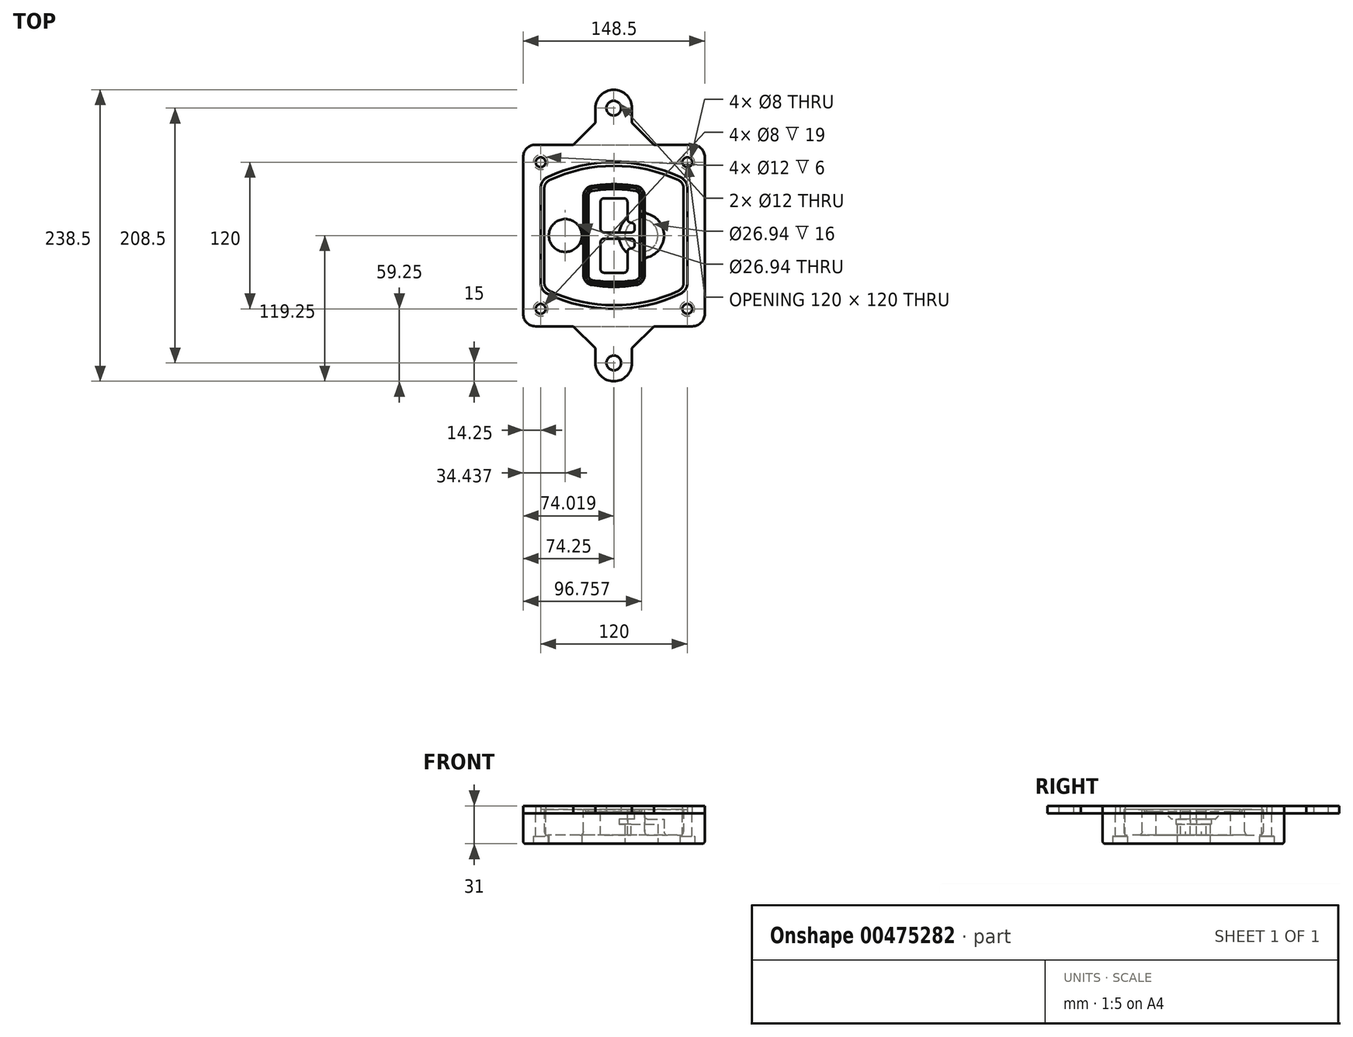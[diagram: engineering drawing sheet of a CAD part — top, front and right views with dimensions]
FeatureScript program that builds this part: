
annotation { "Feature Type Name" : "Feature", "Feature Type Description" : "" }
export const myFeature = defineFeature(function(context is Context, id is Id, definition is map)
    precondition{}
    {
        {
            var Q0;
            Q0=qCreatedBy(makeId("Top.planeOp"),FACE);
            var sketch = newSketch(context, id + "F0", { "sketchPlane" : qUnion([Q0])});
            skPoint(sketch, "E0.rect.middle", {"position": v(0, 0) * mm});
            skLineSegment(sketch, "E1.bottom", {"start": v(-64.25, -74.25) * mm, "end": v(64.25, -74.25) * mm});
            skLineSegment(sketch, "E1.top", {"start": v(-64.25, 74.25) * mm, "end": v(64.25, 74.25) * mm});
            skLineSegment(sketch, "E1.left", {"start": v(-74.25, -64.25) * mm, "end": v(-74.25, 64.25) * mm});
            skLineSegment(sketch, "E1.right", {"start": v(74.25, -64.25) * mm, "end": v(74.25, 64.25) * mm});
            skLineSegment(sketch, "E2", {"start": v(-74.25, 74.25) * mm, "end": v(74.25, -74.25) * mm, "construction": true});
            skLineSegment(sketch, "E3", {"start": v(74.25, 74.25) * mm, "end": v(-74.25, -74.25) * mm, "construction": true});
            skCircle(sketch, "E4", {"center": v(-60, 60) * mm, "radius": 4 * mm});
            skCircle(sketch, "E5", {"center": v(60, 60) * mm, "radius": 4 * mm});
            skCircle(sketch, "E6", {"center": v(60, -60) * mm, "radius": 4 * mm});
            skCircle(sketch, "E7", {"center": v(-60, -60) * mm, "radius": 4 * mm});
            skLineSegment(sketch, "E8", {"start": v(-60, 60) * mm, "end": v(60, 60) * mm, "construction": true});
            skLineSegment(sketch, "E9", {"start": v(60, 60) * mm, "end": v(60, -60) * mm, "construction": true});
            skLineSegment(sketch, "E10", {"start": v(60, -60) * mm, "end": v(-60, -60) * mm, "construction": true});
            skLineSegment(sketch, "E11", {"start": v(-60, -60) * mm, "end": v(-60, 60) * mm, "construction": true});
            skLineSegment(sketch, "E12", {"start": v(-60, 38.83) * mm, "end": v(-60, -38.83) * mm});
            skLineSegment(sketch, "E13", {"start": v(60, 38.83) * mm, "end": v(60, -38.83) * mm});
            skArc(sketch, "E14", {"start": v(54.26, 47.88) * mm, "mid": v(0, 60) * mm, "end": v(-54.26, 47.88) * mm});
            skArc(sketch, "E15", {"start": v(-54.26, -47.88) * mm, "mid": v(0, -60) * mm, "end": v(54.26, -47.88) * mm});
            skLineSegment(sketch, "E16", {"start": v(-60, 0) * mm, "end": v(60, 0) * mm, "construction": true});
            skPoint(sketch, "E17.visualSharp", {"position": v(-60, -45) * mm});
            skArc(sketch, "E17.filletArc", {"start": v(-60, -38.83) * mm, "mid": v(-58.44, -44.2) * mm, "end": v(-54.26, -47.88) * mm});
            skPoint(sketch, "E18.visualSharp", {"position": v(-60, 45) * mm});
            skArc(sketch, "E18.filletArc", {"start": v(-54.26, 47.88) * mm, "mid": v(-58.44, 44.2) * mm, "end": v(-60, 38.83) * mm});
            skPoint(sketch, "E19.visualSharp", {"position": v(60, 45) * mm});
            skArc(sketch, "E19.filletArc", {"start": v(60, 38.83) * mm, "mid": v(58.44, 44.2) * mm, "end": v(54.26, 47.88) * mm});
            skPoint(sketch, "E20.visualSharp", {"position": v(60, -45) * mm});
            skArc(sketch, "E20.filletArc", {"start": v(54.26, -47.88) * mm, "mid": v(58.44, -44.2) * mm, "end": v(60, -38.83) * mm});
            skPoint(sketch, "E21.visualSharp", {"position": v(-74.25, 74.25) * mm});
            skArc(sketch, "E21.filletArc", {"start": v(-64.25, 74.25) * mm, "mid": v(-71.32, 71.32) * mm, "end": v(-74.25, 64.25) * mm});
            skPoint(sketch, "E22.visualSharp", {"position": v(74.25, 74.25) * mm});
            skArc(sketch, "E22.filletArc", {"start": v(74.25, 64.25) * mm, "mid": v(71.32, 71.32) * mm, "end": v(64.25, 74.25) * mm});
            skPoint(sketch, "E23.visualSharp", {"position": v(74.25, -74.25) * mm});
            skArc(sketch, "E23.filletArc", {"start": v(64.25, -74.25) * mm, "mid": v(71.32, -71.32) * mm, "end": v(74.25, -64.25) * mm});
            skPoint(sketch, "E24.visualSharp", {"position": v(-74.25, -74.25) * mm});
            skArc(sketch, "E24.filletArc", {"start": v(-74.25, -64.25) * mm, "mid": v(-71.32, -71.32) * mm, "end": v(-64.25, -74.25) * mm});
            skArc(sketch, "E25.0", {"start": v(57, 38.83) * mm, "mid": v(55.9, 42.58) * mm, "end": v(52.98, 45.17) * mm});
            skLineSegment(sketch, "E25.1", {"start": v(57, 38.83) * mm, "end": v(57, -38.83) * mm});
            skArc(sketch, "E25.2", {"start": v(52.98, -45.17) * mm, "mid": v(55.9, -42.58) * mm, "end": v(57, -38.83) * mm});
            skArc(sketch, "E25.3", {"start": v(-52.98, -45.17) * mm, "mid": v(0, -57) * mm, "end": v(52.98, -45.17) * mm});
            skArc(sketch, "E25.4", {"start": v(-57, -38.83) * mm, "mid": v(-55.9, -42.58) * mm, "end": v(-52.98, -45.17) * mm});
            skArc(sketch, "E25.5", {"start": v(52.98, 45.17) * mm, "mid": v(0, 57) * mm, "end": v(-52.98, 45.17) * mm});
            skLineSegment(sketch, "E25.6", {"start": v(-57, 38.83) * mm, "end": v(-57, -38.83) * mm});
            skArc(sketch, "E25.7", {"start": v(-52.98, 45.17) * mm, "mid": v(-55.9, 42.58) * mm, "end": v(-57, 38.83) * mm});
            skArc(sketch, "E26.0", {"start": v(-55.96, 51.5) * mm, "mid": v(-61.82, 46.33) * mm, "end": v(-64, 38.83) * mm});
            skArc(sketch, "E26.1", {"start": v(55.96, 51.5) * mm, "mid": v(0, 64) * mm, "end": v(-55.96, 51.5) * mm});
            skArc(sketch, "E26.2", {"start": v(64, 38.83) * mm, "mid": v(61.82, 46.33) * mm, "end": v(55.96, 51.5) * mm});
            skLineSegment(sketch, "E26.3", {"start": v(64, 38.83) * mm, "end": v(64, -38.83) * mm});
            skArc(sketch, "E26.4", {"start": v(55.96, -51.5) * mm, "mid": v(61.82, -46.33) * mm, "end": v(64, -38.83) * mm});
            skLineSegment(sketch, "E26.5", {"start": v(-64, 38.83) * mm, "end": v(-64, -38.83) * mm});
            skArc(sketch, "E26.6", {"start": v(-55.96, -51.5) * mm, "mid": v(0, -64) * mm, "end": v(55.96, -51.5) * mm});
            skArc(sketch, "E26.7", {"start": v(-64, -38.83) * mm, "mid": v(-61.82, -46.33) * mm, "end": v(-55.96, -51.5) * mm});
            skSolve(sketch);
        }
        {
            var Q0;
            Q0=makeQuery(id+"F0.imprint","IMPRINT",FACE,{"disambiguationData":[TD([[makeQuery(id+"F0.imprint","IMPRINT",EDGE,{"derivedFrom":sQuery(id+"F0.wireOp",EDGE,"E1.bottom")}),1.0]])]});
            var Q1;
            Q1=makeQuery(id+"F0.imprint","IMPRINT",FACE,{"disambiguationData":[TD([[makeQuery(id+"F0.imprint","IMPRINT",EDGE,{"derivedFrom":sQuery(id+"F0.wireOp",EDGE,"E12")}),1.0]])]});
            var Q2;
            Q2=makeQuery(id+"F0.imprint","IMPRINT",FACE,{"disambiguationData":[TD([[makeQuery(id+"F0.imprint","IMPRINT",EDGE,{"derivedFrom":sQuery(id+"F0.wireOp",EDGE,"E25.0")}),1.0]])]});
            var Q3;
            Q3=makeQuery(id+"F0.imprint","IMPRINT",FACE,{"disambiguationData":[TD([[makeQuery(id+"F0.imprint","IMPRINT",EDGE,{"derivedFrom":sQuery(id+"F0.wireOp",EDGE,"E12")}),-1.0]])]});
            extrude(context, id + "F1", {"entities" : qUnion([Q0, Q1, Q2, Q3]), "oppositeDirection" : true, "depth" : 25 * mm});
        }
        {
            var Q0;
            Q0=makeQuery(id+"F0.imprint","IMPRINT",FACE,{"disambiguationData":[TD([[makeQuery(id+"F0.imprint","IMPRINT",EDGE,{"derivedFrom":sQuery(id+"F0.wireOp",EDGE,"E12")}),1.0]])]});
            extrude(context, id + "F2", {"entities" : qUnion([Q0]), "operationType" : NewBodyOperationType.ADD, "depth" : 3 * mm});
        }
        {
            var Q0;
            Q0=makeQuery(id+"F0.imprint","IMPRINT",FACE,{"disambiguationData":[TD([[makeQuery(id+"F0.imprint","IMPRINT",EDGE,{"derivedFrom":sQuery(id+"F0.wireOp",EDGE,"E25.0")}),1.0]])]});
            extrude(context, id + "F3", {"entities" : qUnion([Q0]), "operationType" : NewBodyOperationType.REMOVE, "oppositeDirection" : true, "depth" : 18 * mm});
        }
        {
            var Q0;
            Q0=makeQuery(id+"F2.opExtrude","CAP_FACE",FACE,{"disambiguationData":[OSD([sQuery(id+"F0.wireOp",EDGE,"E12"),sQuery(id+"F0.wireOp",EDGE,"E13"),sQuery(id+"F0.wireOp",EDGE,"E14"),sQuery(id+"F0.wireOp",EDGE,"E15"),sQuery(id+"F0.wireOp",EDGE,"E17.filletArc"),sQuery(id+"F0.wireOp",EDGE,"E18.filletArc"),sQuery(id+"F0.wireOp",EDGE,"E19.filletArc"),sQuery(id+"F0.wireOp",EDGE,"E20.filletArc"),sQuery(id+"F0.wireOp",EDGE,"E25.0"),sQuery(id+"F0.wireOp",EDGE,"E25.1"),sQuery(id+"F0.wireOp",EDGE,"E25.2"),sQuery(id+"F0.wireOp",EDGE,"E25.3"),sQuery(id+"F0.wireOp",EDGE,"E25.4"),sQuery(id+"F0.wireOp",EDGE,"E25.5"),sQuery(id+"F0.wireOp",EDGE,"E25.6"),sQuery(id+"F0.wireOp",EDGE,"E25.7")])],"isStart":false});
            var sketch = newSketch(context, id + "F4", { "sketchPlane" : qUnion([Q0])});
            skArc(sketch, "E27.0", {"start": v(-18.34, -40.45) * mm, "mid": v(0, -42) * mm, "end": v(18.34, -40.45) * mm});
            skArc(sketch, "E28.0", {"start": v(18.34, 40.45) * mm, "mid": v(0, 42) * mm, "end": v(-18.34, 40.45) * mm});
            skLineSegment(sketch, "E29", {"start": v(-25, 32.57) * mm, "end": v(-25, -32.57) * mm});
            skLineSegment(sketch, "E30", {"start": v(25, 32.57) * mm, "end": v(25, -32.57) * mm});
            skLineSegment(sketch, "E31", {"start": v(-25, 39.1) * mm, "end": v(25, 39.1) * mm, "construction": true});
            skLineSegment(sketch, "E32", {"start": v(-25, -39.1) * mm, "end": v(25, -39.1) * mm, "construction": true});
            skPoint(sketch, "E33.visualSharp", {"position": v(-25, 39.1) * mm});
            skArc(sketch, "E33.filletArc", {"start": v(-18.34, 40.45) * mm, "mid": v(-23.11, 37.73) * mm, "end": v(-25, 32.57) * mm});
            skPoint(sketch, "E34.visualSharp", {"position": v(25, 39.1) * mm});
            skArc(sketch, "E34.filletArc", {"start": v(25, 32.57) * mm, "mid": v(23.11, 37.73) * mm, "end": v(18.34, 40.45) * mm});
            skPoint(sketch, "E35.visualSharp", {"position": v(25, -39.1) * mm});
            skArc(sketch, "E35.filletArc", {"start": v(18.34, -40.45) * mm, "mid": v(23.11, -37.73) * mm, "end": v(25, -32.57) * mm});
            skPoint(sketch, "E36.visualSharp", {"position": v(-25, -39.1) * mm});
            skArc(sketch, "E36.filletArc", {"start": v(-25, -32.57) * mm, "mid": v(-23.11, -37.73) * mm, "end": v(-18.34, -40.45) * mm});
            skArc(sketch, "E37.0", {"start": v(52.98, 45.17) * mm, "mid": v(0, 57) * mm, "end": v(-52.98, 45.17) * mm});
            skArc(sketch, "E37.1", {"start": v(-52.98, 45.17) * mm, "mid": v(-55.9, 42.58) * mm, "end": v(-57, 38.83) * mm});
            skLineSegment(sketch, "E37.2", {"start": v(-57, 38.83) * mm, "end": v(-57, -38.83) * mm});
            skArc(sketch, "E37.3", {"start": v(-57, -38.83) * mm, "mid": v(-55.9, -42.58) * mm, "end": v(-52.98, -45.17) * mm});
            skArc(sketch, "E37.4", {"start": v(-52.98, -45.17) * mm, "mid": v(0, -57) * mm, "end": v(52.98, -45.17) * mm});
            skArc(sketch, "E37.5", {"start": v(52.98, -45.17) * mm, "mid": v(55.9, -42.58) * mm, "end": v(57, -38.83) * mm});
            skLineSegment(sketch, "E37.6", {"start": v(57, 38.83) * mm, "end": v(57, -38.83) * mm});
            skArc(sketch, "E37.7", {"start": v(57, 38.83) * mm, "mid": v(55.9, 42.58) * mm, "end": v(52.98, 45.17) * mm});
            skLineSegment(sketch, "E38.0", {"start": v(23, 32.57) * mm, "end": v(23, -32.57) * mm});
            skArc(sketch, "E38.1", {"start": v(18, -38.48) * mm, "mid": v(21.58, -36.44) * mm, "end": v(23, -32.57) * mm});
            skArc(sketch, "E38.2", {"start": v(-18, -38.48) * mm, "mid": v(0, -40) * mm, "end": v(18, -38.48) * mm});
            skArc(sketch, "E38.3", {"start": v(-23, -32.57) * mm, "mid": v(-21.58, -36.44) * mm, "end": v(-18, -38.48) * mm});
            skLineSegment(sketch, "E38.4", {"start": v(-23, 32.57) * mm, "end": v(-23, -32.57) * mm});
            skArc(sketch, "E38.5", {"start": v(23, 32.57) * mm, "mid": v(21.58, 36.44) * mm, "end": v(18, 38.48) * mm});
            skArc(sketch, "E38.6", {"start": v(-18, 38.48) * mm, "mid": v(-21.58, 36.44) * mm, "end": v(-23, 32.57) * mm});
            skArc(sketch, "E38.7", {"start": v(18, 38.48) * mm, "mid": v(0, 40) * mm, "end": v(-18, 38.48) * mm});
            skArc(sketch, "E39.0", {"start": v(21, 32.57) * mm, "mid": v(20.06, 35.15) * mm, "end": v(17.67, 36.5) * mm});
            skLineSegment(sketch, "E39.1", {"start": v(21, 32.57) * mm, "end": v(21, -32.57) * mm});
            skArc(sketch, "E39.2", {"start": v(17.67, -36.5) * mm, "mid": v(20.06, -35.15) * mm, "end": v(21, -32.57) * mm});
            skArc(sketch, "E39.3", {"start": v(-17.67, -36.5) * mm, "mid": v(0, -38) * mm, "end": v(17.67, -36.5) * mm});
            skArc(sketch, "E39.4", {"start": v(-21, -32.57) * mm, "mid": v(-20.06, -35.15) * mm, "end": v(-17.67, -36.5) * mm});
            skArc(sketch, "E39.5", {"start": v(17.67, 36.5) * mm, "mid": v(0, 38) * mm, "end": v(-17.67, 36.5) * mm});
            skLineSegment(sketch, "E39.6", {"start": v(-21, 32.57) * mm, "end": v(-21, -32.57) * mm});
            skArc(sketch, "E39.7", {"start": v(-17.67, 36.5) * mm, "mid": v(-20.06, 35.15) * mm, "end": v(-21, 32.57) * mm});
            skLineSegment(sketch, "E40", {"start": v(-25, 0) * mm, "end": v(25, 0) * mm, "construction": true});
            skLineSegment(sketch, "E41", {"start": v(-11, 5.5) * mm, "end": v(-11, 27.5) * mm});
            skLineSegment(sketch, "E42", {"start": v(-8, 30.5) * mm, "end": v(8, 30.5) * mm});
            skLineSegment(sketch, "E43", {"start": v(11, 27.5) * mm, "end": v(11, 13.5) * mm});
            skLineSegment(sketch, "E44", {"start": v(14, 10.5) * mm, "end": v(14, 10.5) * mm});
            skLineSegment(sketch, "E45", {"start": v(17, 7.5) * mm, "end": v(17, 5.5) * mm});
            skLineSegment(sketch, "E46", {"start": v(14, 2.5) * mm, "end": v(-8, 2.5) * mm});
            skPoint(sketch, "E47.visualSharp", {"position": v(-11, 30.5) * mm});
            skArc(sketch, "E47.filletArc", {"start": v(-8, 30.5) * mm, "mid": v(-10.12, 29.62) * mm, "end": v(-11, 27.5) * mm});
            skPoint(sketch, "E48.visualSharp", {"position": v(11, 30.5) * mm});
            skArc(sketch, "E48.filletArc", {"start": v(11, 27.5) * mm, "mid": v(10.12, 29.62) * mm, "end": v(8, 30.5) * mm});
            skPoint(sketch, "E49.visualSharp", {"position": v(11, 10.5) * mm});
            skArc(sketch, "E49.filletArc", {"start": v(11, 13.5) * mm, "mid": v(11.88, 11.38) * mm, "end": v(14, 10.5) * mm});
            skPoint(sketch, "E50.visualSharp", {"position": v(17, 10.5) * mm});
            skArc(sketch, "E50.filletArc", {"start": v(17, 7.5) * mm, "mid": v(16.12, 9.62) * mm, "end": v(14, 10.5) * mm});
            skPoint(sketch, "E51.visualSharp", {"position": v(17, 2.5) * mm});
            skArc(sketch, "E51.filletArc", {"start": v(14, 2.5) * mm, "mid": v(16.12, 3.38) * mm, "end": v(17, 5.5) * mm});
            skPoint(sketch, "E52.visualSharp", {"position": v(-11, 2.5) * mm});
            skArc(sketch, "E52.filletArc", {"start": v(-11, 5.5) * mm, "mid": v(-10.12, 3.38) * mm, "end": v(-8, 2.5) * mm});
            skLineSegment(sketch, "E53.0.MirrorCS", {"start": v(14, -2.5) * mm, "end": v(-8, -2.5) * mm});
            skArc(sketch, "E54.0.MirrorCS", {"start": v(-11, -5.5) * mm, "mid": v(-10.12, -3.38) * mm, "end": v(-8, -2.5) * mm});
            skLineSegment(sketch, "E55.0.MirrorCS", {"start": v(-11, -5.5) * mm, "end": v(-11, -27.5) * mm});
            skArc(sketch, "E56.0.MirrorCS", {"start": v(-8, -30.5) * mm, "mid": v(-10.12, -29.62) * mm, "end": v(-11, -27.5) * mm});
            skLineSegment(sketch, "E57.0.MirrorCS", {"start": v(-8, -30.5) * mm, "end": v(8, -30.5) * mm});
            skArc(sketch, "E58.0.MirrorCS", {"start": v(11, -27.5) * mm, "mid": v(10.12, -29.62) * mm, "end": v(8, -30.5) * mm});
            skLineSegment(sketch, "E59.0.MirrorCS", {"start": v(11, -27.5) * mm, "end": v(11, -13.5) * mm});
            skArc(sketch, "E60.0.MirrorCS", {"start": v(11, -13.5) * mm, "mid": v(11.88, -11.38) * mm, "end": v(14, -10.5) * mm});
            skArc(sketch, "E61.0.MirrorCS", {"start": v(17, -7.5) * mm, "mid": v(16.12, -9.62) * mm, "end": v(14, -10.5) * mm});
            skLineSegment(sketch, "E62.0.MirrorCS", {"start": v(17, -7.5) * mm, "end": v(17, -5.5) * mm});
            skArc(sketch, "E63.0.MirrorCS", {"start": v(14, -2.5) * mm, "mid": v(16.12, -3.38) * mm, "end": v(17, -5.5) * mm});
            skSolve(sketch);
        }
        {
            var Q0;
            Q0=makeQuery(id+"F4.imprint","IMPRINT",FACE,{"disambiguationData":[TD([[makeQuery(id+"F4.imprint","IMPRINT",EDGE,{"derivedFrom":sQuery(id+"F4.wireOp",EDGE,"E27.0")}),1.0]])]});
            var Q1;
            Q1=makeQuery(id+"F4.imprint","IMPRINT",FACE,{"disambiguationData":[TD([[makeQuery(id+"F4.imprint","IMPRINT",EDGE,{"derivedFrom":sQuery(id+"F4.wireOp",EDGE,"E38.0")}),-1.0]])]});
            var Q2;
            Q2=makeQuery(id+"F4.imprint","IMPRINT",FACE,{"disambiguationData":[TD([[makeQuery(id+"F4.imprint","IMPRINT",EDGE,{"derivedFrom":sQuery(id+"F4.wireOp",EDGE,"E39.0")}),1.0]])]});
            extrude(context, id + "F5", {"entities" : qUnion([Q0, Q1, Q2]), "operationType" : NewBodyOperationType.ADD, "endBound" : BoundingType.UP_TO_NEXT, "oppositeDirection" : true, "depth" : 25 * mm});
        }
        {
            var Q0;
            Q0=makeQuery(id+"F4.imprint","IMPRINT",FACE,{"disambiguationData":[TD([[makeQuery(id+"F4.imprint","IMPRINT",EDGE,{"derivedFrom":sQuery(id+"F4.wireOp",EDGE,"E38.0")}),-1.0]])]});
            extrude(context, id + "F6", {"entities" : qUnion([Q0]), "operationType" : NewBodyOperationType.REMOVE, "oppositeDirection" : true, "depth" : 2 * mm});
        }
        {
            var Q0;
            Q0=makeQuery(id+"F1.opExtrude","CAP_FACE",FACE,{"disambiguationData":[OSD([sQuery(id+"F0.wireOp",EDGE,"E1.bottom"),sQuery(id+"F0.wireOp",EDGE,"E1.top"),sQuery(id+"F0.wireOp",EDGE,"E1.left"),sQuery(id+"F0.wireOp",EDGE,"E1.right"),sQuery(id+"F0.wireOp",EDGE,"E4"),sQuery(id+"F0.wireOp",EDGE,"E5"),sQuery(id+"F0.wireOp",EDGE,"E6"),sQuery(id+"F0.wireOp",EDGE,"E7"),sQuery(id+"F0.wireOp",EDGE,"E21.filletArc"),sQuery(id+"F0.wireOp",EDGE,"E22.filletArc"),sQuery(id+"F0.wireOp",EDGE,"E23.filletArc"),sQuery(id+"F0.wireOp",EDGE,"E24.filletArc")])],"isStart":false});
            var sketch = newSketch(context, id + "F7", { "sketchPlane" : qUnion([Q0])});
            skCircle(sketch, "E64", {"center": v(22.5, 0) * mm, "radius": 13.47 * mm});
            skCircle(sketch, "E65", {"center": v(-39.81, 0) * mm, "radius": 13.47 * mm});
            skLineSegment(sketch, "E66", {"start": v(74.25, 0) * mm, "end": v(-74.25, 0) * mm});
            skCircle(sketch, "E67", {"center": v(22.5, 0) * mm, "radius": 18.47 * mm});
            skCircle(sketch, "E68", {"center": v(60, -60) * mm, "radius": 6 * mm});
            skCircle(sketch, "E69", {"center": v(-60, -60) * mm, "radius": 6 * mm});
            skCircle(sketch, "E70", {"center": v(-60, 60) * mm, "radius": 6 * mm});
            skCircle(sketch, "E71", {"center": v(60, 60) * mm, "radius": 6 * mm});
            skSolve(sketch);
        }
        {
            var Q0;
            {var subQ1=sQuery(id+"F7.wireOp",EDGE,"E66");var subQ4=sQuery(id+"F7.wireOp",EDGE,"E64");var subQ6=makeQuery(id+"F7.imprint","INTERSECT",VERTEX,{"disambiguationData":[OD(0.0)],"derivedFrom":[subQ4,subQ1]});Q0=makeQuery(id+"F7.imprint","IMPRINT",FACE,{"disambiguationData":[TD([[makeQuery(id+"F7.imprint","IMPRINT",EDGE,{"disambiguationData":[TD([[subQ6,-1.0]])],"derivedFrom":subQ4}),-1.0]])]});}
            var Q1;
            {var subQ0=sQuery(id+"F7.wireOp",EDGE,"E66");var subQ1=sQuery(id+"F7.wireOp",EDGE,"E64");var subQ3=makeQuery(id+"F7.imprint","INTERSECT",VERTEX,{"disambiguationData":[OD(0.0)],"derivedFrom":[subQ1,subQ0]});Q1=makeQuery(id+"F7.imprint","IMPRINT",FACE,{"disambiguationData":[TD([[makeQuery(id+"F7.imprint","IMPRINT",EDGE,{"disambiguationData":[TD([[subQ3,-1.0]])],"derivedFrom":subQ1}),1.0]])]});}
            var Q2;
            {var subQ0=sQuery(id+"F7.wireOp",EDGE,"E66");var subQ1=sQuery(id+"F7.wireOp",EDGE,"E64");var subQ3=makeQuery(id+"F7.imprint","INTERSECT",VERTEX,{"disambiguationData":[OD(0.0)],"derivedFrom":[subQ1,subQ0]});Q2=makeQuery(id+"F7.imprint","IMPRINT",FACE,{"disambiguationData":[TD([[makeQuery(id+"F7.imprint","IMPRINT",EDGE,{"disambiguationData":[TD([[subQ3,1.0]])],"derivedFrom":subQ1}),1.0]])]});}
            var Q3;
            {var subQ1=sQuery(id+"F7.wireOp",EDGE,"E66");var subQ4=sQuery(id+"F7.wireOp",EDGE,"E64");var subQ6=makeQuery(id+"F7.imprint","INTERSECT",VERTEX,{"disambiguationData":[OD(0.0)],"derivedFrom":[subQ4,subQ1]});Q3=makeQuery(id+"F7.imprint","IMPRINT",FACE,{"disambiguationData":[TD([[makeQuery(id+"F7.imprint","IMPRINT",EDGE,{"disambiguationData":[TD([[subQ6,1.0]])],"derivedFrom":subQ4}),-1.0]])]});}
            extrude(context, id + "F8", {"entities" : qUnion([Q0, Q1, Q2, Q3]), "operationType" : NewBodyOperationType.ADD, "oppositeDirection" : true, "depth" : 20 * mm});
        }
        {
            var Q0;
            {var subQ0=sQuery(id+"F7.wireOp",EDGE,"E66");var subQ1=sQuery(id+"F7.wireOp",EDGE,"E64");var subQ3=makeQuery(id+"F7.imprint","INTERSECT",VERTEX,{"disambiguationData":[OD(0.0)],"derivedFrom":[subQ1,subQ0]});Q0=makeQuery(id+"F7.imprint","IMPRINT",FACE,{"disambiguationData":[TD([[makeQuery(id+"F7.imprint","IMPRINT",EDGE,{"disambiguationData":[TD([[subQ3,-1.0]])],"derivedFrom":subQ1}),1.0]])]});}
            var Q1;
            {var subQ0=sQuery(id+"F7.wireOp",EDGE,"E66");var subQ1=sQuery(id+"F7.wireOp",EDGE,"E64");var subQ3=makeQuery(id+"F7.imprint","INTERSECT",VERTEX,{"disambiguationData":[OD(0.0)],"derivedFrom":[subQ1,subQ0]});Q1=makeQuery(id+"F7.imprint","IMPRINT",FACE,{"disambiguationData":[TD([[makeQuery(id+"F7.imprint","IMPRINT",EDGE,{"disambiguationData":[TD([[subQ3,1.0]])],"derivedFrom":subQ1}),1.0]])]});}
            extrude(context, id + "F9", {"entities" : qUnion([Q0, Q1]), "operationType" : NewBodyOperationType.REMOVE, "oppositeDirection" : true, "depth" : 16 * mm});
        }
        {
            var Q0;
            {var subQ0=sQuery(id+"F7.wireOp",EDGE,"E66");var subQ1=sQuery(id+"F7.wireOp",EDGE,"E65");var subQ3=makeQuery(id+"F7.imprint","INTERSECT",VERTEX,{"disambiguationData":[OD(0.0)],"derivedFrom":[subQ1,subQ0]});Q0=makeQuery(id+"F7.imprint","IMPRINT",FACE,{"disambiguationData":[TD([[makeQuery(id+"F7.imprint","IMPRINT",EDGE,{"disambiguationData":[TD([[subQ3,-1.0]])],"derivedFrom":subQ1}),1.0]])]});}
            var Q1;
            {var subQ0=sQuery(id+"F7.wireOp",EDGE,"E66");var subQ1=sQuery(id+"F7.wireOp",EDGE,"E65");var subQ3=makeQuery(id+"F7.imprint","INTERSECT",VERTEX,{"disambiguationData":[OD(0.0)],"derivedFrom":[subQ1,subQ0]});Q1=makeQuery(id+"F7.imprint","IMPRINT",FACE,{"disambiguationData":[TD([[makeQuery(id+"F7.imprint","IMPRINT",EDGE,{"disambiguationData":[TD([[subQ3,1.0]])],"derivedFrom":subQ1}),1.0]])]});}
            extrude(context, id + "F10", {"entities" : qUnion([Q0, Q1]), "operationType" : NewBodyOperationType.REMOVE, "oppositeDirection" : true, "depth" : 25 * mm});
        }
        {
            var Q0;
            Q0=makeQuery(id+"F7.imprint","IMPRINT",FACE,{"disambiguationData":[TD([[makeQuery(id+"F7.imprint","IMPRINT",EDGE,{"derivedFrom":sQuery(id+"F7.wireOp",EDGE,"E68")}),1.0]])]});
            var Q1;
            Q1=makeQuery(id+"F7.imprint","IMPRINT",FACE,{"disambiguationData":[TD([[makeQuery(id+"F7.imprint","IMPRINT",EDGE,{"derivedFrom":makeQuery(id+"F1.opExtrude","CAP_EDGE",EDGE,{"disambiguationData":[OSD([sQuery(id+"F0.wireOp",EDGE,"E5")])],"isStart":false})}),-1.0]])]});
            var Q2;
            Q2=makeQuery(id+"F7.imprint","IMPRINT",FACE,{"disambiguationData":[TD([[makeQuery(id+"F7.imprint","IMPRINT",EDGE,{"derivedFrom":sQuery(id+"F7.wireOp",EDGE,"E69")}),1.0]])]});
            var Q3;
            Q3=makeQuery(id+"F7.imprint","IMPRINT",FACE,{"disambiguationData":[TD([[makeQuery(id+"F7.imprint","IMPRINT",EDGE,{"derivedFrom":makeQuery(id+"F1.opExtrude","CAP_EDGE",EDGE,{"disambiguationData":[OSD([sQuery(id+"F0.wireOp",EDGE,"E4")])],"isStart":false})}),-1.0]])]});
            var Q4;
            Q4=makeQuery(id+"F7.imprint","IMPRINT",FACE,{"disambiguationData":[TD([[makeQuery(id+"F7.imprint","IMPRINT",EDGE,{"derivedFrom":sQuery(id+"F7.wireOp",EDGE,"E70")}),1.0]])]});
            var Q5;
            Q5=makeQuery(id+"F7.imprint","IMPRINT",FACE,{"disambiguationData":[TD([[makeQuery(id+"F7.imprint","IMPRINT",EDGE,{"derivedFrom":makeQuery(id+"F1.opExtrude","CAP_EDGE",EDGE,{"disambiguationData":[OSD([sQuery(id+"F0.wireOp",EDGE,"E7")])],"isStart":false})}),-1.0]])]});
            var Q6;
            Q6=makeQuery(id+"F7.imprint","IMPRINT",FACE,{"disambiguationData":[TD([[makeQuery(id+"F7.imprint","IMPRINT",EDGE,{"derivedFrom":sQuery(id+"F7.wireOp",EDGE,"E71")}),1.0]])]});
            var Q7;
            Q7=makeQuery(id+"F7.imprint","IMPRINT",FACE,{"disambiguationData":[TD([[makeQuery(id+"F7.imprint","IMPRINT",EDGE,{"derivedFrom":makeQuery(id+"F1.opExtrude","CAP_EDGE",EDGE,{"disambiguationData":[OSD([sQuery(id+"F0.wireOp",EDGE,"E6")])],"isStart":false})}),-1.0]])]});
            extrude(context, id + "F11", {"entities" : qUnion([Q0, Q1, Q2, Q3, Q4, Q5, Q6, Q7]), "operationType" : NewBodyOperationType.REMOVE, "oppositeDirection" : true, "depth" : 6 * mm});
        }
        {
            var Q0;
            Q0=makeQuery(id+"F9.boolean.opBoolean","COPY",FACE,{"derivedFrom":makeQuery(id+"F9.opExtrude","CAP_FACE",FACE,{"disambiguationData":[OSD([sQuery(id+"F7.wireOp",EDGE,"E64")])],"isStart":false})});
            var sketch = newSketch(context, id + "F12", { "sketchPlane" : qUnion([Q0])});
            skArc(sketch, "E72.0", {"start": v(11, 14.45) * mm, "mid": v(6.45, 9.13) * mm, "end": v(4.2, 2.5) * mm});
            skArc(sketch, "E72.1", {"start": v(4.2, -2.5) * mm, "mid": v(6.45, -9.13) * mm, "end": v(11, -14.45) * mm});
            skLineSegment(sketch, "E73", {"start": v(4.2, -2.5) * mm, "end": v(14, -2.5) * mm});
            skLineSegment(sketch, "E74.0", {"start": v(14, 2.5) * mm, "end": v(4.2, 2.5) * mm});
            skArc(sketch, "E74.1", {"start": v(14, 2.5) * mm, "mid": v(16.12, 3.38) * mm, "end": v(17, 5.5) * mm});
            skLineSegment(sketch, "E74.2", {"start": v(17, 7.5) * mm, "end": v(17, 5.5) * mm});
            skArc(sketch, "E74.3", {"start": v(17, 7.5) * mm, "mid": v(16.12, 9.62) * mm, "end": v(14, 10.5) * mm});
            skArc(sketch, "E74.4", {"start": v(11, 13.5) * mm, "mid": v(11.88, 11.38) * mm, "end": v(14, 10.5) * mm});
            skLineSegment(sketch, "E74.5", {"start": v(11, 14.45) * mm, "end": v(11, 13.5) * mm});
            skLineSegment(sketch, "E74.7", {"start": v(14, -2.5) * mm, "end": v(4.2, -2.5) * mm});
            skArc(sketch, "E74.8", {"start": v(14, -2.5) * mm, "mid": v(16.12, -3.38) * mm, "end": v(17, -5.5) * mm});
            skLineSegment(sketch, "E74.9", {"start": v(17, -7.5) * mm, "end": v(17, -5.5) * mm});
            skArc(sketch, "E74.10", {"start": v(17, -7.5) * mm, "mid": v(16.12, -9.62) * mm, "end": v(14, -10.5) * mm});
            skArc(sketch, "E74.11", {"start": v(11, -13.5) * mm, "mid": v(11.88, -11.38) * mm, "end": v(14, -10.5) * mm});
            skLineSegment(sketch, "E74.12", {"start": v(11, -14.45) * mm, "end": v(11, -13.5) * mm});
            skPoint(sketch, "E75.orphan", {"position": v(11, -27.5) * mm});
            skPoint(sketch, "E76.orphan", {"position": v(-8, -2.5) * mm});
            skPoint(sketch, "E77.orphan", {"position": v(-8, 2.5) * mm});
            skPoint(sketch, "E78.orphan", {"position": v(11, 27.5) * mm});
            skSolve(sketch);
        }
        {
            var Q0;
            {var subQ7=sQuery(id+"F12.wireOp",EDGE,"E72.0");var subQ14=sQuery(id+"F12.wireOp",EDGE,"E72.1");var subQ16=sQuery(id+"F12.wireOp",EDGE,"E74.1");var subQ18=sQuery(id+"F12.wireOp",EDGE,"E74.8");Q0=qUnion([makeQuery(id+"F12.imprint","IMPRINT",FACE,{"disambiguationData":[TD([[makeQuery(id+"F12.imprint","IMPRINT",EDGE,{"derivedFrom":subQ7}),1.0]])]}),makeQuery(id+"F12.imprint","IMPRINT",FACE,{"disambiguationData":[TD([[makeQuery(id+"F12.imprint","IMPRINT",EDGE,{"derivedFrom":subQ14}),1.0]])]}),makeQuery(id+"F12.imprint","IMPRINT",FACE,{"disambiguationData":[TD([[makeQuery(id+"F12.imprint","IMPRINT",EDGE,{"derivedFrom":subQ16}),1.0]])]}),makeQuery(id+"F12.imprint","IMPRINT",FACE,{"disambiguationData":[TD([[makeQuery(id+"F12.imprint","IMPRINT",EDGE,{"derivedFrom":subQ18}),-1.0]])]})]);}
            var Q1;
            Q1=makeQuery(id+"F5.boolean.opBoolean","SPLIT",FACE,{"disambiguationData":[TD([makeQuery(id+"F5.opExtrude","SWEPT_FACE",FACE,{"disambiguationData":[OSD([sQuery(id+"F4.wireOp",EDGE,"E41")])]})])],"derivedFrom":makeQuery(id+"F3.boolean.opBoolean","COPY",FACE,{"derivedFrom":makeQuery(id+"F3.opExtrude","CAP_FACE",FACE,{"disambiguationData":[OSD([sQuery(id+"F0.wireOp",EDGE,"E25.0"),sQuery(id+"F0.wireOp",EDGE,"E25.1"),sQuery(id+"F0.wireOp",EDGE,"E25.2"),sQuery(id+"F0.wireOp",EDGE,"E25.3"),sQuery(id+"F0.wireOp",EDGE,"E25.4"),sQuery(id+"F0.wireOp",EDGE,"E25.5"),sQuery(id+"F0.wireOp",EDGE,"E25.6"),sQuery(id+"F0.wireOp",EDGE,"E25.7")])],"isStart":false})})});
            extrude(context, id + "F13", {"entities" : qUnion([Q0]), "operationType" : NewBodyOperationType.REMOVE, "endBound" : BoundingType.UP_TO_SURFACE, "endBoundEntityFace" : qUnion([Q1]), "depth" : 25 * mm});
        }
        {
            var Q0;
            Q0=makeQuery(id+"F3.boolean.opBoolean","COPY",EDGE,{"derivedFrom":makeQuery(id+"F3.opExtrude","CAP_EDGE",EDGE,{"disambiguationData":[OSD([sQuery(id+"F0.wireOp",EDGE,"E25.6")])],"isStart":false})});
            var Q1;
            Q1=makeQuery(id+"F8.boolean.opBoolean","INTERSECT",EDGE,{"derivedFrom":[makeQuery(id+"F5.opExtrude","SWEPT_FACE",FACE,{"disambiguationData":[OSD([sQuery(id+"F4.wireOp",EDGE,"E30")])]}),makeQuery(id+"F8.opExtrude","CAP_FACE",FACE,{"disambiguationData":[OSD([sQuery(id+"F7.wireOp",EDGE,"E67")])],"isStart":false})]});
            var Q2;
            Q2=makeQuery(id+"F8.boolean.opBoolean","INTERSECT",EDGE,{"disambiguationData":[OD(1.0)],"derivedFrom":[makeQuery(id+"F5.opExtrude","SWEPT_FACE",FACE,{"disambiguationData":[OSD([sQuery(id+"F4.wireOp",EDGE,"E30")])]}),makeQuery(id+"F8.opExtrude","SWEPT_FACE",FACE,{"disambiguationData":[OSD([sQuery(id+"F7.wireOp",EDGE,"E67")])]})]});
            var Q3;
            {var subQ0=sQuery(id+"F4.wireOp",EDGE,"E30");Q3=makeQuery(id+"F8.boolean.opBoolean","SPLIT",EDGE,{"disambiguationData":[TD([makeQuery(id+"F5.opExtrude","SWEPT_FACE",FACE,{"disambiguationData":[OSD([sQuery(id+"F4.wireOp",EDGE,"E35.filletArc")])]})])],"derivedFrom":makeQuery(id+"F5.opExtrude","CAP_EDGE",EDGE,{"disambiguationData":[OSD([subQ0])],"isStart":false})});}
            var Q4;
            {var subQ0=sQuery(id+"F0.wireOp",EDGE,"E25.7");var subQ1=sQuery(id+"F0.wireOp",EDGE,"E25.1");var subQ2=sQuery(id+"F0.wireOp",EDGE,"E25.6");var subQ3=sQuery(id+"F0.wireOp",EDGE,"E25.5");var subQ4=sQuery(id+"F0.wireOp",EDGE,"E25.4");var subQ5=sQuery(id+"F0.wireOp",EDGE,"E25.0");var subQ6=sQuery(id+"F0.wireOp",EDGE,"E25.2");var subQ7=sQuery(id+"F0.wireOp",EDGE,"E25.3");Q4=makeQuery(id+"F8.boolean.opBoolean","INTERSECT",EDGE,{"derivedFrom":[makeQuery(id+"F5.boolean.opBoolean","SPLIT",FACE,{"disambiguationData":[TD([makeQuery(id+"F2.opExtrude","SWEPT_FACE",FACE,{"disambiguationData":[OSD([subQ5])]})])],"derivedFrom":makeQuery(id+"F3.boolean.opBoolean","COPY",FACE,{"derivedFrom":makeQuery(id+"F3.opExtrude","CAP_FACE",FACE,{"disambiguationData":[OSD([subQ5,subQ1,subQ6,subQ7,subQ4,subQ3,subQ2,subQ0])],"isStart":false})})}),makeQuery(id+"F8.opExtrude","SWEPT_FACE",FACE,{"disambiguationData":[OSD([sQuery(id+"F7.wireOp",EDGE,"E67")])]})]});}
            var Q5;
            Q5=makeQuery(id+"F8.boolean.opBoolean","INTERSECT",EDGE,{"disambiguationData":[OD(0.0)],"derivedFrom":[makeQuery(id+"F5.opExtrude","SWEPT_FACE",FACE,{"disambiguationData":[OSD([sQuery(id+"F4.wireOp",EDGE,"E30")])]}),makeQuery(id+"F8.opExtrude","SWEPT_FACE",FACE,{"disambiguationData":[OSD([sQuery(id+"F7.wireOp",EDGE,"E67")])]})]});
            fillet(context, id + "F14", {"entities" : qUnion([Q0, Q1, Q2, Q3, Q4, Q5]), "radius" : 3 * mm, "tangentPropagation" : true, "allowEdgeOverflow" : false});
        }
        {
            var Q0;
            Q0=makeQuery(id+"F1.opExtrude","CAP_EDGE",EDGE,{"disambiguationData":[OSD([sQuery(id+"F0.wireOp",EDGE,"E1.bottom")])],"isStart":false});
            fillet(context, id + "F15", {"entities" : qUnion([Q0]), "radius" : 2 * mm, "tangentPropagation" : true, "allowEdgeOverflow" : false});
        }
        {
            var Q0;
            Q0=qCreatedBy(makeId("Top.planeOp"),FACE);
            var sketch = newSketch(context, id + "F16", { "sketchPlane" : qUnion([Q0])});
            skLineSegment(sketch, "E79.0", {"start": v(-64.25, 74.25) * mm, "end": v(64.25, 74.25) * mm});
            skArc(sketch, "E79.1", {"start": v(-64.25, 74.25) * mm, "mid": v(-71.32, 71.32) * mm, "end": v(-74.25, 64.25) * mm});
            skLineSegment(sketch, "E79.2", {"start": v(-74.25, -64.25) * mm, "end": v(-74.25, 64.25) * mm});
            skArc(sketch, "E79.3", {"start": v(-74.25, -64.25) * mm, "mid": v(-71.32, -71.32) * mm, "end": v(-64.25, -74.25) * mm});
            skLineSegment(sketch, "E79.4", {"start": v(-64.25, -74.25) * mm, "end": v(64.25, -74.25) * mm});
            skArc(sketch, "E79.5", {"start": v(64.25, -74.25) * mm, "mid": v(71.32, -71.32) * mm, "end": v(74.25, -64.25) * mm});
            skLineSegment(sketch, "E79.6", {"start": v(74.25, -64.25) * mm, "end": v(74.25, 64.25) * mm});
            skArc(sketch, "E79.7", {"start": v(74.25, 64.25) * mm, "mid": v(71.32, 71.32) * mm, "end": v(64.25, 74.25) * mm});
            skCircle(sketch, "E79.8", {"center": v(60, 60) * mm, "radius": 4 * mm});
            skCircle(sketch, "E79.9", {"center": v(-60, 60) * mm, "radius": 4 * mm});
            skCircle(sketch, "E79.10", {"center": v(-60, -60) * mm, "radius": 4 * mm});
            skCircle(sketch, "E79.11", {"center": v(60, -60) * mm, "radius": 4 * mm});
            skArc(sketch, "E79.12", {"start": v(-54.26, -47.88) * mm, "mid": v(0, -60) * mm, "end": v(54.26, -47.88) * mm});
            skLineSegment(sketch, "E79.13", {"start": v(60, 38.83) * mm, "end": v(60, -38.83) * mm});
            skArc(sketch, "E79.14", {"start": v(54.26, 47.88) * mm, "mid": v(0, 60) * mm, "end": v(-54.26, 47.88) * mm});
            skArc(sketch, "E79.15", {"start": v(60, 38.83) * mm, "mid": v(58.44, 44.2) * mm, "end": v(54.26, 47.88) * mm});
            skArc(sketch, "E79.16", {"start": v(-54.26, 47.88) * mm, "mid": v(-58.44, 44.2) * mm, "end": v(-60, 38.83) * mm});
            skLineSegment(sketch, "E79.17", {"start": v(-60, 38.83) * mm, "end": v(-60, -38.83) * mm});
            skArc(sketch, "E79.18", {"start": v(54.26, -47.88) * mm, "mid": v(58.44, -44.2) * mm, "end": v(60, -38.83) * mm});
            skArc(sketch, "E79.19", {"start": v(-60, -38.83) * mm, "mid": v(-58.44, -44.2) * mm, "end": v(-54.26, -47.88) * mm});
            skPoint(sketch, "E80.endSnap0", {"position": v(0, 74.25) * mm});
            skLineSegment(sketch, "E81", {"start": v(-33.23, 74.25) * mm, "end": v(-15.23, 92.25) * mm});
            skLineSegment(sketch, "E82", {"start": v(-15.23, 92.25) * mm, "end": v(-15.23, 104.25) * mm});
            skLineSegment(sketch, "E83", {"start": v(32.77, 74.25) * mm, "end": v(14.77, 92.25) * mm});
            skLineSegment(sketch, "E84", {"start": v(14.77, 92.25) * mm, "end": v(14.77, 104.25) * mm});
            skArc(sketch, "E85", {"start": v(14.77, 104.25) * mm, "mid": v(-0.23, 119.25) * mm, "end": v(-15.23, 104.25) * mm});
            skCircle(sketch, "E86", {"center": v(-0.23, 104.25) * mm, "radius": 6 * mm});
            skPoint(sketch, "E87.endSnap0", {"position": v(74.25, 0) * mm});
            skLineSegment(sketch, "E88.MirrorCS", {"start": v(32.77, -74.25) * mm, "end": v(14.77, -92.25) * mm});
            skLineSegment(sketch, "E89.MirrorCS", {"start": v(14.77, -92.25) * mm, "end": v(14.77, -104.25) * mm});
            skArc(sketch, "E90.MirrorCS", {"start": v(14.77, -104.25) * mm, "mid": v(-0.23, -119.25) * mm, "end": v(-15.23, -104.25) * mm});
            skCircle(sketch, "E91.MirrorC", {"center": v(-0.23, -104.25) * mm, "radius": 6 * mm});
            skLineSegment(sketch, "E92.MirrorCS", {"start": v(-15.23, -92.25) * mm, "end": v(-15.23, -104.25) * mm});
            skLineSegment(sketch, "E93.MirrorCS", {"start": v(-33.23, -74.25) * mm, "end": v(-15.23, -92.25) * mm});
            skSolve(sketch);
        }
        {
            var Q0;
            {var subQ1=sQuery(id+"F16.wireOp",EDGE,"E79.1");Q0=makeQuery(id+"F16.imprint","IMPRINT",FACE,{"disambiguationData":[TD([[makeQuery(id+"F16.imprint","IMPRINT",EDGE,{"derivedFrom":subQ1}),1.0]])]});}
            var Q1;
            {var subQ0=sQuery(id+"F16.wireOp",EDGE,"E88.MirrorCS");Q1=makeQuery(id+"F16.imprint","IMPRINT",FACE,{"disambiguationData":[TD([[makeQuery(id+"F16.imprint","IMPRINT",EDGE,{"derivedFrom":subQ0}),-1.0]])]});}
            var Q2;
            {var subQ0=sQuery(id+"F16.wireOp",EDGE,"E81");Q2=makeQuery(id+"F16.imprint","IMPRINT",FACE,{"disambiguationData":[TD([[makeQuery(id+"F16.imprint","IMPRINT",EDGE,{"derivedFrom":subQ0}),-1.0]])]});}
            extrude(context, id + "F17", {"entities" : qUnion([Q0, Q1, Q2]), "depth" : 6 * mm});
        }
    });
